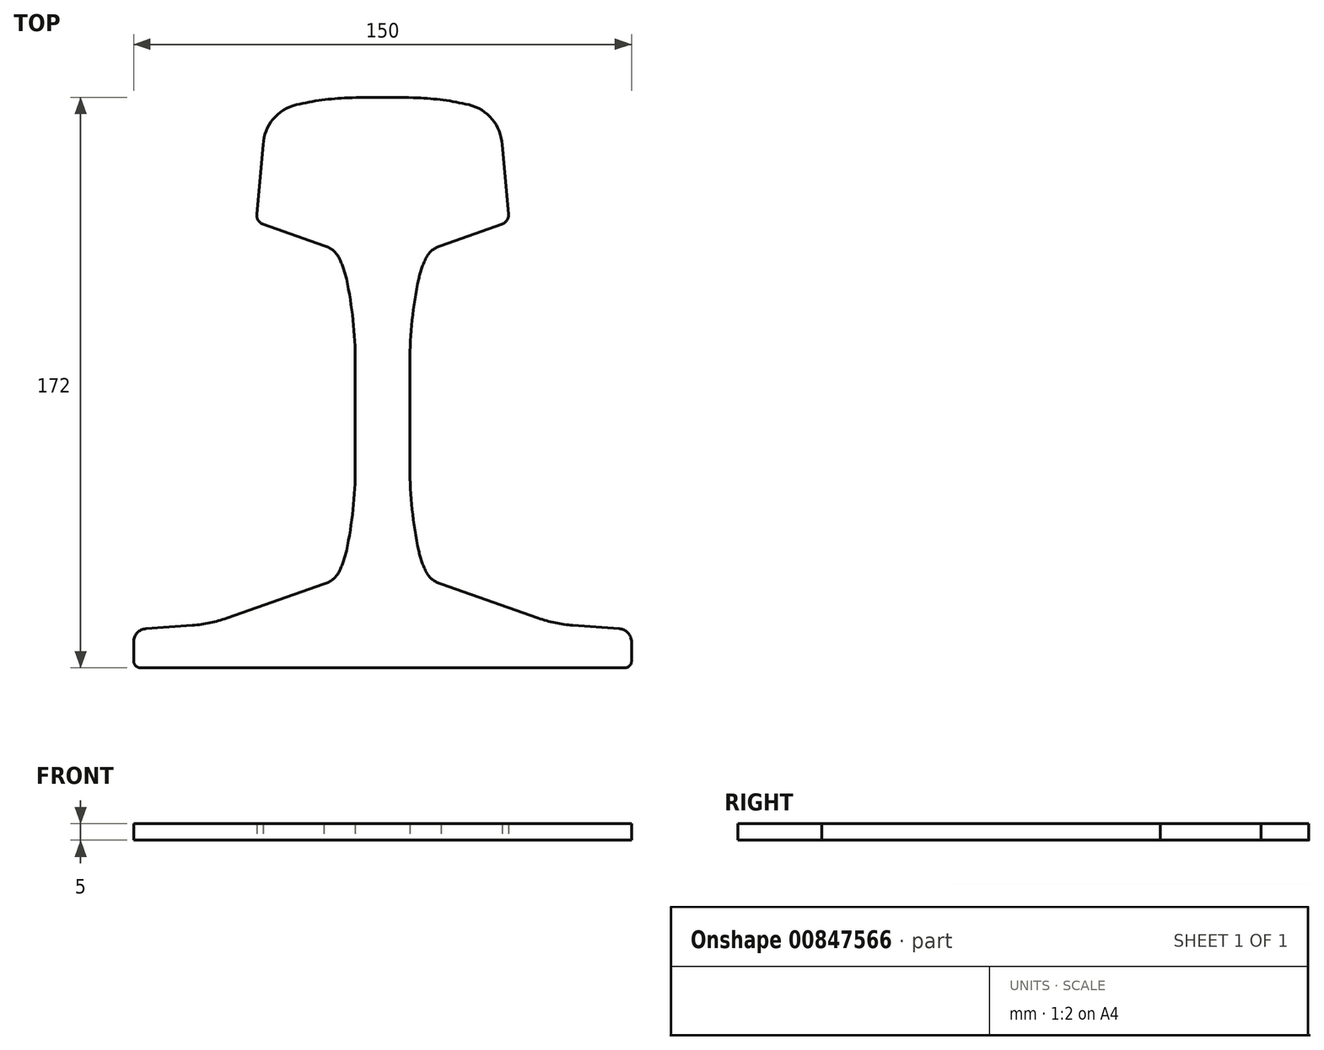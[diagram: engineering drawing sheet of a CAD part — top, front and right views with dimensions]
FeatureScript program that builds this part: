
annotation { "Feature Type Name" : "Feature", "Feature Type Description" : "" }
export const myFeature = defineFeature(function(context is Context, id is Id, definition is map)
    precondition{}
    {
        {
            var Q0;
            Q0=qCreatedBy(makeId("Top.planeOp"),FACE);
            var sketch = newSketch(context, id + "F0", { "sketchPlane" : qUnion([Q0])});
            skArc(sketch, "E0.0.0", {"start": v(40.43, 100.47) * mm, "mid": v(37.44, 108.16) * mm, "end": v(30.43, 112.5) * mm});
            skArc(sketch, "E0.0.1", {"start": v(30.43, 112.5) * mm, "mid": v(22.73, 113.92) * mm, "end": v(14.93, 114.59) * mm});
            skArc(sketch, "E0.0.2", {"start": v(14.93, 114.59) * mm, "mid": v(4.43, 114.77) * mm, "end": v(-6.07, 114.59) * mm});
            skArc(sketch, "E0.0.3", {"start": v(-6.07, 114.59) * mm, "mid": v(-13.87, 113.92) * mm, "end": v(-21.57, 112.5) * mm});
            skArc(sketch, "E0.0.4", {"start": v(-21.57, 112.5) * mm, "mid": v(-28.58, 108.16) * mm, "end": v(-31.57, 100.47) * mm});
            skFitSpline(sketch, "E0.0.5", {"points": [v(-31.57, 100.47) * mm, v(-32.2, 93.5) * mm, v(-32.85, 86.53) * mm, v(-33.49, 79.56) * mm]});
            skArc(sketch, "E0.0.6", {"start": v(-33.49, 79.56) * mm, "mid": v(-33.03, 77.67) * mm, "end": v(-31.5, 76.46) * mm});
            skFitSpline(sketch, "E0.0.7", {"points": [v(-31.5, 76.46) * mm, v(-25.4, 74.3) * mm, v(-19.3, 72.15) * mm, v(-13.2, 70) * mm]});
            skArc(sketch, "E0.0.8", {"start": v(-13.2, 70) * mm, "mid": v(-10.57, 68.68) * mm, "end": v(-8.72, 66.4) * mm});
            skArc(sketch, "E0.0.9", {"start": v(-8.72, 66.4) * mm, "mid": v(-7.37, 63.25) * mm, "end": v(-6.44, 59.96) * mm});
            skArc(sketch, "E0.0.10", {"start": v(-6.44, 59.96) * mm, "mid": v(-4.48, 47.56) * mm, "end": v(-3.82, 35.02) * mm});
            skFitSpline(sketch, "E0.0.11", {"points": [v(-3.82, 35.02) * mm, v(-3.82, 24.35) * mm, v(-3.82, 13.69) * mm, v(-3.82, 3.02) * mm]});
            skArc(sketch, "E0.0.12", {"start": v(-3.82, 3.02) * mm, "mid": v(-4.48, -9.52) * mm, "end": v(-6.44, -21.92) * mm});
            skArc(sketch, "E0.0.13", {"start": v(-6.44, -21.92) * mm, "mid": v(-7.37, -25.21) * mm, "end": v(-8.72, -28.36) * mm});
            skArc(sketch, "E0.0.14", {"start": v(-8.72, -28.36) * mm, "mid": v(-10.57, -30.64) * mm, "end": v(-13.2, -31.95) * mm});
            skFitSpline(sketch, "E0.0.15", {"points": [v(-13.2, -31.95) * mm, v(-22.94, -35.4) * mm, v(-32.68, -38.83) * mm, v(-42.42, -42.27) * mm]});
            skArc(sketch, "E0.0.16", {"start": v(-42.42, -42.27) * mm, "mid": v(-47.57, -43.71) * mm, "end": v(-52.87, -44.45) * mm});
            skFitSpline(sketch, "E0.0.17", {"points": [v(-52.87, -44.45) * mm, v(-57.53, -44.8) * mm, v(-62.2, -45.13) * mm, v(-66.86, -45.46) * mm]});
            skArc(sketch, "E0.0.18", {"start": v(-66.86, -45.46) * mm, "mid": v(-69.5, -46.73) * mm, "end": v(-70.57, -49.45) * mm});
            skFitSpline(sketch, "E0.0.19", {"points": [v(-70.57, -49.45) * mm, v(-70.57, -51.38) * mm, v(-70.57, -53.3) * mm, v(-70.57, -55.23) * mm]});
            skArc(sketch, "E0.0.20", {"start": v(-70.57, -55.23) * mm, "mid": v(-69.98, -56.64) * mm, "end": v(-68.57, -57.23) * mm});
            skFitSpline(sketch, "E0.0.21", {"points": [v(-68.57, -57.23) * mm, v(-44.24, -57.23) * mm, v(-19.9, -57.23) * mm, v(4.43, -57.23) * mm]});
            skFitSpline(sketch, "E0.0.22", {"points": [v(4.43, -57.23) * mm, v(28.76, -57.23) * mm, v(53.1, -57.23) * mm, v(77.43, -57.23) * mm]});
            skArc(sketch, "E0.0.23", {"start": v(77.43, -57.23) * mm, "mid": v(78.84, -56.64) * mm, "end": v(79.43, -55.23) * mm});
            skFitSpline(sketch, "E0.0.24", {"points": [v(79.43, -55.23) * mm, v(79.43, -53.3) * mm, v(79.43, -51.38) * mm, v(79.43, -49.45) * mm]});
            skArc(sketch, "E0.0.25", {"start": v(79.43, -49.45) * mm, "mid": v(78.36, -46.73) * mm, "end": v(75.72, -45.46) * mm});
            skFitSpline(sketch, "E0.0.26", {"points": [v(75.72, -45.46) * mm, v(71.05, -45.13) * mm, v(66.39, -44.8) * mm, v(61.73, -44.45) * mm]});
            skArc(sketch, "E0.0.27", {"start": v(61.73, -44.45) * mm, "mid": v(56.43, -43.71) * mm, "end": v(51.28, -42.27) * mm});
            skFitSpline(sketch, "E0.0.28", {"points": [v(51.28, -42.27) * mm, v(41.54, -38.83) * mm, v(31.8, -35.4) * mm, v(22.06, -31.95) * mm]});
            skArc(sketch, "E0.0.29", {"start": v(22.06, -31.95) * mm, "mid": v(19.43, -30.64) * mm, "end": v(17.58, -28.36) * mm});
            skArc(sketch, "E0.0.30", {"start": v(17.58, -28.36) * mm, "mid": v(16.23, -25.21) * mm, "end": v(15.3, -21.92) * mm});
            skArc(sketch, "E0.0.31", {"start": v(15.3, -21.92) * mm, "mid": v(13.34, -9.52) * mm, "end": v(12.68, 3.02) * mm});
            skFitSpline(sketch, "E0.0.32", {"points": [v(12.68, 3.02) * mm, v(12.68, 13.69) * mm, v(12.68, 24.35) * mm, v(12.68, 35.02) * mm]});
            skArc(sketch, "E0.0.33", {"start": v(12.68, 35.02) * mm, "mid": v(13.34, 47.56) * mm, "end": v(15.3, 59.96) * mm});
            skArc(sketch, "E0.0.34", {"start": v(15.3, 59.96) * mm, "mid": v(16.23, 63.25) * mm, "end": v(17.58, 66.4) * mm});
            skArc(sketch, "E0.0.35", {"start": v(17.58, 66.4) * mm, "mid": v(19.43, 68.68) * mm, "end": v(22.06, 70) * mm});
            skFitSpline(sketch, "E0.0.36", {"points": [v(22.06, 70) * mm, v(28.16, 72.15) * mm, v(34.26, 74.3) * mm, v(40.36, 76.46) * mm]});
            skArc(sketch, "E0.0.37", {"start": v(40.36, 76.46) * mm, "mid": v(41.89, 77.67) * mm, "end": v(42.35, 79.56) * mm});
            skFitSpline(sketch, "E0.0.38", {"points": [v(42.35, 79.56) * mm, v(41.7, 86.53) * mm, v(41.07, 93.5) * mm, v(40.43, 100.47) * mm]});
            skSolve(sketch);
        }
        {
            var Q0;
            Q0 = qSketchRegion(id + "F0", true);
            extrude(context, id + "F1", {"entities" : qUnion([Q0]), "depth" : 5 * mm, "offsetDistance" : 25 * mm});
        }
    });
